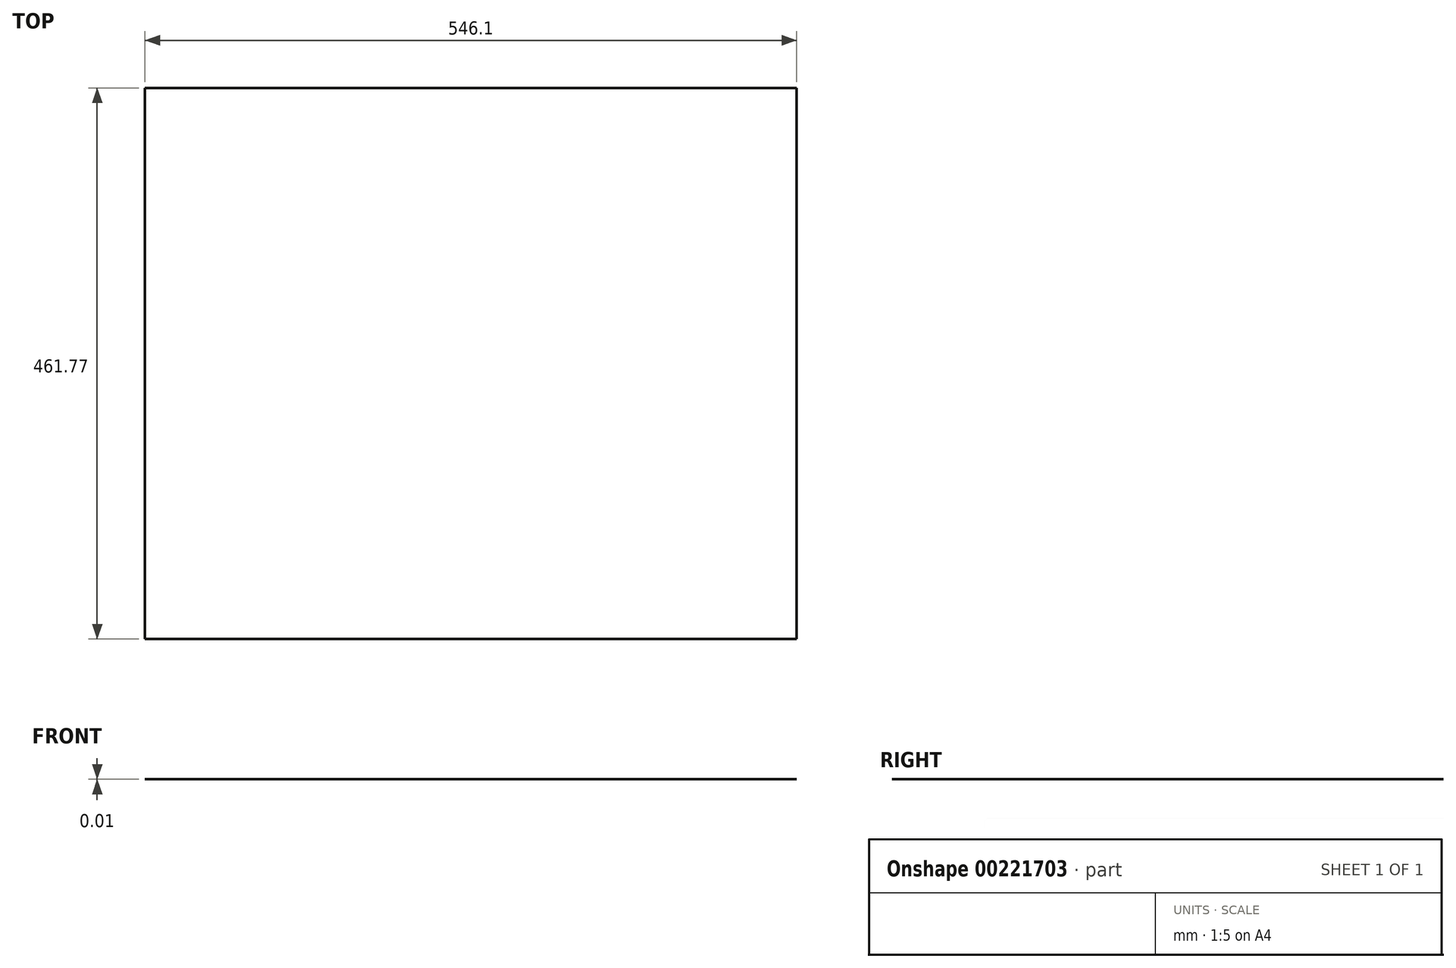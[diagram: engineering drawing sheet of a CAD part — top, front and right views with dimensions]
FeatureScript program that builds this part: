
annotation { "Feature Type Name" : "Feature", "Feature Type Description" : "" }
export const myFeature = defineFeature(function(context is Context, id is Id, definition is map)
    precondition{}
    {
        {
            var Q0;
            Q0=qCreatedBy(makeId("Top.planeOp"),FACE);
            var sketch = newSketch(context, id + "F0", { "sketchPlane" : qUnion([Q0])});
            skLineSegment(sketch, "E0.bottom", {"start": v(-294.52, -167.46) * mm, "end": v(251.58, -167.46) * mm});
            skLineSegment(sketch, "E0.top", {"start": v(-294.52, 294.31) * mm, "end": v(251.58, 294.31) * mm});
            skLineSegment(sketch, "E0.left", {"start": v(-294.52, -167.46) * mm, "end": v(-294.52, 294.31) * mm});
            skLineSegment(sketch, "E0.right", {"start": v(251.58, -167.46) * mm, "end": v(251.58, 294.31) * mm});
            skSolve(sketch);
        }
        {
            var Q0;
            Q0 = qSketchRegion(id + "F0", true);
            extrude(context, id + "F1", {"entities" : qUnion([Q0]), "oppositeDirection" : true, "depth" : 3 / 406.4 * mm});
        }
    });
